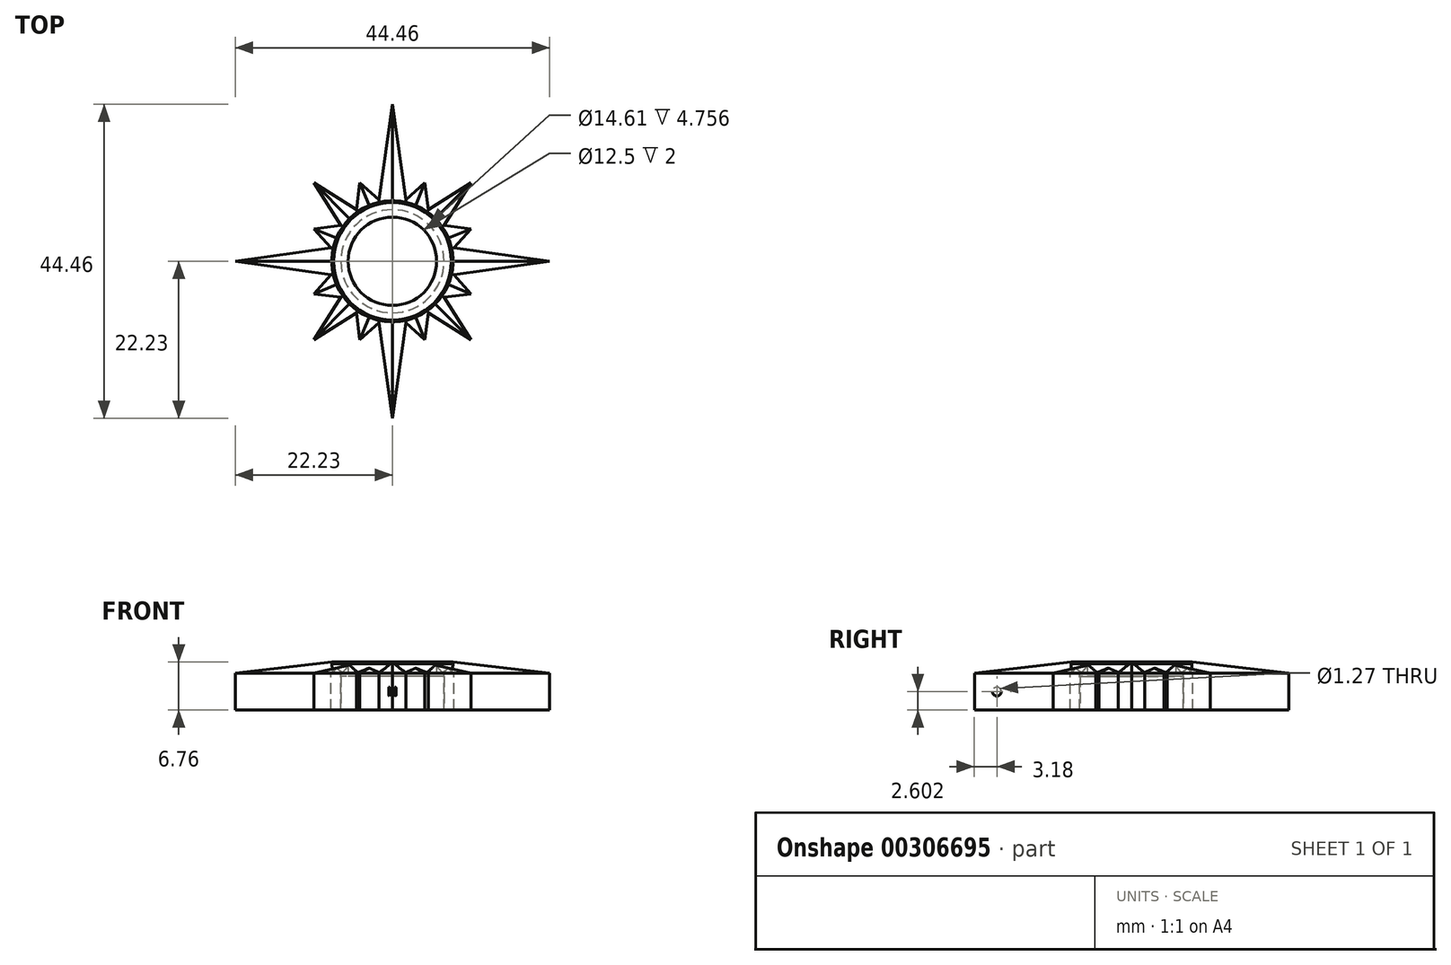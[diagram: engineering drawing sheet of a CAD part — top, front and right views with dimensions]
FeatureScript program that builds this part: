
annotation { "Feature Type Name" : "Feature", "Feature Type Description" : "" }
export const myFeature = defineFeature(function(context is Context, id is Id, definition is map)
    precondition{}
    {
        {
            var Q0;
            Q0=qCreatedBy(makeId("Top.planeOp"),FACE);
            var sketch = newSketch(context, id + "F0", { "sketchPlane" : qUnion([Q0])});
            skCircle(sketch, "E0", {"center": v(0, 0) * mm, "radius": 8.9 * mm, "construction": true});
            skCircle(sketch, "E1", {"center": v(0, 0) * mm, "radius": 12.03 * mm, "construction": true});
            skCircle(sketch, "E2", {"center": v(0, 0) * mm, "radius": 15.72 * mm, "construction": true});
            skCircle(sketch, "E3", {"center": v(0, 0) * mm, "radius": 22.23 * mm, "construction": true});
            skLineSegment(sketch, "E4", {"start": v(8.9, 0) * mm, "end": v(22.23, 0) * mm, "construction": true});
            skLineSegment(sketch, "E5", {"start": v(0, 0) * mm, "end": v(0, 22.23) * mm, "construction": true});
            skLineSegment(sketch, "E6", {"start": v(4.72, 21.72) * mm, "end": v(0, 0) * mm, "construction": true});
            skLineSegment(sketch, "E7", {"start": v(0, 0) * mm, "end": v(8.5, 20.53) * mm, "construction": true});
            skLineSegment(sketch, "E8", {"start": v(12.67, 18.26) * mm, "end": v(0, 0) * mm, "construction": true});
            skLineSegment(sketch, "E9", {"start": v(15.72, 15.72) * mm, "end": v(0, 0) * mm, "construction": true});
            skLineSegment(sketch, "E10", {"start": v(0, 22.23) * mm, "end": v(1.89, 8.69) * mm});
            skLineSegment(sketch, "E11", {"start": v(1.89, 8.69) * mm, "end": v(4.6, 11.11) * mm});
            skLineSegment(sketch, "E12", {"start": v(4.6, 11.11) * mm, "end": v(5.07, 7.3) * mm});
            skLineSegment(sketch, "E13", {"start": v(5.07, 7.3) * mm, "end": v(11.11, 11.11) * mm});
            skLineSegment(sketch, "E14.MirrorCS", {"start": v(7.3, 5.07) * mm, "end": v(11.11, 11.11) * mm});
            skLineSegment(sketch, "E15.MirrorCS", {"start": v(11.11, 4.6) * mm, "end": v(7.3, 5.07) * mm});
            skLineSegment(sketch, "E16.MirrorCS", {"start": v(22.23, 0) * mm, "end": v(8.69, 1.89) * mm});
            skLineSegment(sketch, "E17.MirrorCS", {"start": v(8.69, 1.89) * mm, "end": v(11.11, 4.6) * mm});
            skLineSegment(sketch, "E18.MirrorCS", {"start": v(0, -22.23) * mm, "end": v(1.89, -8.69) * mm});
            skLineSegment(sketch, "E19.MirrorCS", {"start": v(1.89, -8.69) * mm, "end": v(4.6, -11.11) * mm});
            skLineSegment(sketch, "E20.MirrorCS", {"start": v(4.6, -11.11) * mm, "end": v(5.07, -7.3) * mm});
            skLineSegment(sketch, "E21.MirrorCS", {"start": v(5.07, -7.3) * mm, "end": v(11.11, -11.11) * mm});
            skLineSegment(sketch, "E22.MirrorCS", {"start": v(7.3, -5.07) * mm, "end": v(11.11, -11.11) * mm});
            skLineSegment(sketch, "E23.MirrorCS", {"start": v(11.11, -4.6) * mm, "end": v(7.3, -5.07) * mm});
            skLineSegment(sketch, "E24.MirrorCS", {"start": v(22.23, 0) * mm, "end": v(8.69, -1.89) * mm});
            skLineSegment(sketch, "E25.MirrorCS", {"start": v(8.69, -1.89) * mm, "end": v(11.11, -4.6) * mm});
            skLineSegment(sketch, "E26.MirrorCS", {"start": v(0, -22.23) * mm, "end": v(-1.89, -8.69) * mm});
            skLineSegment(sketch, "E27.MirrorCS", {"start": v(-1.89, -8.69) * mm, "end": v(-4.6, -11.11) * mm});
            skLineSegment(sketch, "E28.MirrorCS", {"start": v(-4.6, -11.11) * mm, "end": v(-5.07, -7.3) * mm});
            skLineSegment(sketch, "E29.MirrorCS", {"start": v(-5.07, -7.3) * mm, "end": v(-11.11, -11.11) * mm});
            skLineSegment(sketch, "E30.MirrorCS", {"start": v(-7.3, -5.07) * mm, "end": v(-11.11, -11.11) * mm});
            skLineSegment(sketch, "E31.MirrorCS", {"start": v(-11.11, -4.6) * mm, "end": v(-7.3, -5.07) * mm});
            skLineSegment(sketch, "E32.MirrorCS", {"start": v(-8.69, -1.89) * mm, "end": v(-11.11, -4.6) * mm});
            skLineSegment(sketch, "E33.MirrorCS", {"start": v(-22.23, 0) * mm, "end": v(-8.69, -1.89) * mm});
            skLineSegment(sketch, "E34.MirrorCS", {"start": v(-22.23, 0) * mm, "end": v(-8.69, 1.89) * mm});
            skLineSegment(sketch, "E35.MirrorCS", {"start": v(-8.69, 1.89) * mm, "end": v(-11.11, 4.6) * mm});
            skLineSegment(sketch, "E36.MirrorCS", {"start": v(-11.11, 4.6) * mm, "end": v(-7.3, 5.07) * mm});
            skLineSegment(sketch, "E37.MirrorCS", {"start": v(-7.3, 5.07) * mm, "end": v(-11.11, 11.11) * mm});
            skLineSegment(sketch, "E38.MirrorCS", {"start": v(-5.07, 7.3) * mm, "end": v(-11.11, 11.11) * mm});
            skLineSegment(sketch, "E39.MirrorCS", {"start": v(-4.6, 11.11) * mm, "end": v(-5.07, 7.3) * mm});
            skLineSegment(sketch, "E40.MirrorCS", {"start": v(0, 22.23) * mm, "end": v(-1.89, 8.69) * mm});
            skLineSegment(sketch, "E41.MirrorCS", {"start": v(-1.89, 8.69) * mm, "end": v(-4.6, 11.11) * mm});
            skLineSegment(sketch, "E42", {"start": v(4.6, 11.11) * mm, "end": v(11.11, 11.11) * mm, "construction": true});
            skLineSegment(sketch, "E43", {"start": v(0, 22.23) * mm, "end": v(11.11, 11.11) * mm, "construction": true});
            skSolve(sketch);
        }
        {
            var Q0;
            Q0=qCreatedBy(makeId("Top.planeOp"),FACE);
            cPlane(context, id + "F1", {"entities" : qUnion([Q0]), "cplaneType" : CPlaneType.OFFSET, "offset" : 2.54 * mm, "width" : 152.4 * mm, "height" : 152.4 * mm});
        }
        {
            var Q0;
            Q0=qCreatedBy(id+"F1.planeOp",FACE);
            var sketch = newSketch(context, id + "F2", { "sketchPlane" : qUnion([Q0])});
            skPoint(sketch, "E44", {"position": v(0, 0) * mm});
            skSolve(sketch);
        }
        {
            var Q0;
            Q0=sQuery(id+"F2.wireOp",VERTEX,"E44");
            var Q1;
            Q1=makeQuery(id+"F0.imprint","IMPRINT",FACE,{"disambiguationData":[TD([[makeQuery(id+"F0.imprint","IMPRINT",EDGE,{"derivedFrom":sQuery(id+"F0.wireOp",EDGE,"E10")}),-1.0]])]});
            loft(context, id + "F3", {"sheetProfilesArray" : [{ "sheetProfileEntities" : qUnion([Q0]) }, { "sheetProfileEntities" : qUnion([Q1]) }]});
        }
        {
            var Q0;
            Q0=makeQuery(id+"F3.opLoft","CAP_FACE",FACE,{"disambiguationData":[OSD([makeQuery(id+"F0.imprint","IMPRINT",FACE,{"disambiguationData":[TD([[makeQuery(id+"F0.imprint","IMPRINT",EDGE,{"derivedFrom":sQuery(id+"F0.wireOp",EDGE,"E10")}),-1.0]])]})])],"isStart":true});
            var sketch = newSketch(context, id + "F4", { "sketchPlane" : qUnion([Q0])});
            skCircle(sketch, "E45", {"center": v(0, 0) * mm, "radius": 8.57 * mm});
            skSolve(sketch);
        }
        {
            var Q0;
            Q0 = qSketchRegion(id + "F4", true);
            extrude(context, id + "F5", {"entities" : qUnion([Q0]), "operationType" : NewBodyOperationType.REMOVE, "endBound" : BoundingType.THROUGH_ALL, "oppositeDirection" : true, "depth" : 25.4 * mm});
        }
        {
            var Q0;
            Q0 = qSketchRegion(id + "F0", true);
            extrude(context, id + "F6", {"entities" : qUnion([Q0]), "operationType" : NewBodyOperationType.ADD, "oppositeDirection" : true, "depth" : 5.2 * mm});
        }
        {
            var Q0;
            Q0=makeQuery(id+"F6.opExtrude","CAP_FACE",FACE,{"disambiguationData":[OSD([sQuery(id+"F0.wireOp",EDGE,"E10"),sQuery(id+"F0.wireOp",EDGE,"E11"),sQuery(id+"F0.wireOp",EDGE,"E12"),sQuery(id+"F0.wireOp",EDGE,"E13"),sQuery(id+"F0.wireOp",EDGE,"E14.MirrorCS"),sQuery(id+"F0.wireOp",EDGE,"E15.MirrorCS"),sQuery(id+"F0.wireOp",EDGE,"E16.MirrorCS"),sQuery(id+"F0.wireOp",EDGE,"E17.MirrorCS"),sQuery(id+"F0.wireOp",EDGE,"E18.MirrorCS"),sQuery(id+"F0.wireOp",EDGE,"E19.MirrorCS"),sQuery(id+"F0.wireOp",EDGE,"E20.MirrorCS"),sQuery(id+"F0.wireOp",EDGE,"E21.MirrorCS"),sQuery(id+"F0.wireOp",EDGE,"E22.MirrorCS"),sQuery(id+"F0.wireOp",EDGE,"E23.MirrorCS"),sQuery(id+"F0.wireOp",EDGE,"E24.MirrorCS"),sQuery(id+"F0.wireOp",EDGE,"E25.MirrorCS"),sQuery(id+"F0.wireOp",EDGE,"E26.MirrorCS"),sQuery(id+"F0.wireOp",EDGE,"E27.MirrorCS"),sQuery(id+"F0.wireOp",EDGE,"E28.MirrorCS"),sQuery(id+"F0.wireOp",EDGE,"E29.MirrorCS"),sQuery(id+"F0.wireOp",EDGE,"E30.MirrorCS"),sQuery(id+"F0.wireOp",EDGE,"E31.MirrorCS"),sQuery(id+"F0.wireOp",EDGE,"E32.MirrorCS"),sQuery(id+"F0.wireOp",EDGE,"E33.MirrorCS"),sQuery(id+"F0.wireOp",EDGE,"E34.MirrorCS"),sQuery(id+"F0.wireOp",EDGE,"E35.MirrorCS"),sQuery(id+"F0.wireOp",EDGE,"E36.MirrorCS"),sQuery(id+"F0.wireOp",EDGE,"E37.MirrorCS"),sQuery(id+"F0.wireOp",EDGE,"E38.MirrorCS"),sQuery(id+"F0.wireOp",EDGE,"E39.MirrorCS"),sQuery(id+"F0.wireOp",EDGE,"E40.MirrorCS"),sQuery(id+"F0.wireOp",EDGE,"E41.MirrorCS")])],"isStart":false});
            var sketch = newSketch(context, id + "F7", { "sketchPlane" : qUnion([Q0])});
            skCircle(sketch, "E46", {"center": v(0, 0) * mm, "radius": 7.3 * mm});
            skSolve(sketch);
        }
        {
            var Q0;
            Q0 = qSketchRegion(id + "F7", true);
            extrude(context, id + "F8", {"entities" : qUnion([Q0]), "operationType" : NewBodyOperationType.REMOVE, "endBound" : BoundingType.THROUGH_ALL, "oppositeDirection" : true, "depth" : 25.4 * mm});
        }
        {
            var Q0;
            Q0=makeQuery(id+"F6.opExtrude","CAP_FACE",FACE,{"disambiguationData":[OSD([sQuery(id+"F0.wireOp",EDGE,"E10"),sQuery(id+"F0.wireOp",EDGE,"E11"),sQuery(id+"F0.wireOp",EDGE,"E12"),sQuery(id+"F0.wireOp",EDGE,"E13"),sQuery(id+"F0.wireOp",EDGE,"E14.MirrorCS"),sQuery(id+"F0.wireOp",EDGE,"E15.MirrorCS"),sQuery(id+"F0.wireOp",EDGE,"E16.MirrorCS"),sQuery(id+"F0.wireOp",EDGE,"E17.MirrorCS"),sQuery(id+"F0.wireOp",EDGE,"E18.MirrorCS"),sQuery(id+"F0.wireOp",EDGE,"E19.MirrorCS"),sQuery(id+"F0.wireOp",EDGE,"E20.MirrorCS"),sQuery(id+"F0.wireOp",EDGE,"E21.MirrorCS"),sQuery(id+"F0.wireOp",EDGE,"E22.MirrorCS"),sQuery(id+"F0.wireOp",EDGE,"E23.MirrorCS"),sQuery(id+"F0.wireOp",EDGE,"E24.MirrorCS"),sQuery(id+"F0.wireOp",EDGE,"E25.MirrorCS"),sQuery(id+"F0.wireOp",EDGE,"E26.MirrorCS"),sQuery(id+"F0.wireOp",EDGE,"E27.MirrorCS"),sQuery(id+"F0.wireOp",EDGE,"E28.MirrorCS"),sQuery(id+"F0.wireOp",EDGE,"E29.MirrorCS"),sQuery(id+"F0.wireOp",EDGE,"E30.MirrorCS"),sQuery(id+"F0.wireOp",EDGE,"E31.MirrorCS"),sQuery(id+"F0.wireOp",EDGE,"E32.MirrorCS"),sQuery(id+"F0.wireOp",EDGE,"E33.MirrorCS"),sQuery(id+"F0.wireOp",EDGE,"E34.MirrorCS"),sQuery(id+"F0.wireOp",EDGE,"E35.MirrorCS"),sQuery(id+"F0.wireOp",EDGE,"E36.MirrorCS"),sQuery(id+"F0.wireOp",EDGE,"E37.MirrorCS"),sQuery(id+"F0.wireOp",EDGE,"E38.MirrorCS"),sQuery(id+"F0.wireOp",EDGE,"E39.MirrorCS"),sQuery(id+"F0.wireOp",EDGE,"E40.MirrorCS"),sQuery(id+"F0.wireOp",EDGE,"E41.MirrorCS")])],"isStart":true});
            var sketch = newSketch(context, id + "F9", { "sketchPlane" : qUnion([Q0])});
            skCircle(sketch, "E47", {"center": v(0, 0) * mm, "radius": 6.25 * mm});
            skCircle(sketch, "E48", {"center": v(0, 0) * mm, "radius": 8.57 * mm});
            skSolve(sketch);
        }
        {
            var Q0;
            Q0 = qSketchRegion(id + "F9", true);
            extrude(context, id + "F10", {"entities" : qUnion([Q0]), "operationType" : NewBodyOperationType.ADD, "depth" : 1.56 * mm, "hasSecondDirection" : true, "secondDirectionOppositeDirection" : true, "secondDirectionDepth" : 2 * mm - (1.56 * mm)});
        }
        {
            var Q0;
            Q0=qCreatedBy(makeId("Right.planeOp"),FACE);
            var sketch = newSketch(context, id + "F11", { "sketchPlane" : qUnion([Q0])});
            skCircle(sketch, "E49", {"center": v(-19.05, -2.6) * mm, "radius": 0.64 * mm});
            skSolve(sketch);
        }
        {
            var Q0;
            Q0 = qSketchRegion(id + "F11", true);
            extrude(context, id + "F12", {"entities" : qUnion([Q0]), "operationType" : NewBodyOperationType.REMOVE, "endBound" : BoundingType.THROUGH_ALL, "depth" : 25.4 * mm, "hasSecondDirection" : true, "secondDirectionBound" : SecondDirectionBoundingType.THROUGH_ALL, "secondDirectionOppositeDirection" : true, "secondDirectionDepth" : 25.4 * mm});
        }
        {
            var Q0;
            {var subQ0=sQuery(id+"F9.wireOp",EDGE,"E48");var subQ1=makeQuery(id+"F10.opExtrude","CAP_FACE",FACE,{"disambiguationData":[OSD([sQuery(id+"F9.wireOp",EDGE,"E47"),subQ0])],"isStart":false});var subQ2=makeQuery(id+"F10.opExtrude","SWEPT_FACE",FACE,{"disambiguationData":[OSD([subQ0])]});Q0=makeQuery(id+"F10.boolean.opBoolean","SPLIT",EDGE,{"disambiguationData":[topologyDisambiguationEdgeConnected([subQ1,subQ2]),TD([makeQuery(id+"F3.opLoft","SWEPT_FACE",FACE,{"disambiguationData":[OSD([sQuery(id+"F0.wireOp",EDGE,"E18.MirrorCS"),sQuery(id+"F0.wireOp",EDGE,"E26.MirrorCS"),sQuery(id+"F0.wireOp",EDGE,"E27.MirrorCS")])]})])],"derivedFrom":makeQuery(id+"F10.opExtrude","CAP_EDGE",EDGE,{"disambiguationData":[OSD([subQ0])],"isStart":false})});}
            var Q1;
            {var subQ0=sQuery(id+"F9.wireOp",EDGE,"E48");var subQ1=makeQuery(id+"F10.opExtrude","CAP_FACE",FACE,{"disambiguationData":[OSD([sQuery(id+"F9.wireOp",EDGE,"E47"),subQ0])],"isStart":false});var subQ2=makeQuery(id+"F10.opExtrude","SWEPT_FACE",FACE,{"disambiguationData":[OSD([subQ0])]});Q1=makeQuery(id+"F10.boolean.opBoolean","SPLIT",EDGE,{"disambiguationData":[topologyDisambiguationEdgeConnected([subQ1,subQ2]),TD([makeQuery(id+"F3.opLoft","SWEPT_FACE",FACE,{"disambiguationData":[OSD([sQuery(id+"F0.wireOp",EDGE,"E16.MirrorCS"),sQuery(id+"F0.wireOp",EDGE,"E24.MirrorCS"),sQuery(id+"F0.wireOp",EDGE,"E25.MirrorCS")])]})])],"derivedFrom":makeQuery(id+"F10.opExtrude","CAP_EDGE",EDGE,{"disambiguationData":[OSD([subQ0])],"isStart":false})});}
            var Q2;
            {var subQ0=sQuery(id+"F9.wireOp",EDGE,"E48");var subQ1=makeQuery(id+"F10.opExtrude","CAP_FACE",FACE,{"disambiguationData":[OSD([sQuery(id+"F9.wireOp",EDGE,"E47"),subQ0])],"isStart":false});var subQ2=makeQuery(id+"F10.opExtrude","SWEPT_FACE",FACE,{"disambiguationData":[OSD([subQ0])]});Q2=makeQuery(id+"F10.boolean.opBoolean","SPLIT",EDGE,{"disambiguationData":[topologyDisambiguationEdgeConnected([subQ1,subQ2]),TD([makeQuery(id+"F3.opLoft","SWEPT_FACE",FACE,{"disambiguationData":[OSD([sQuery(id+"F0.wireOp",EDGE,"E10"),sQuery(id+"F0.wireOp",EDGE,"E11"),sQuery(id+"F0.wireOp",EDGE,"E40.MirrorCS")])]})])],"derivedFrom":makeQuery(id+"F10.opExtrude","CAP_EDGE",EDGE,{"disambiguationData":[OSD([subQ0])],"isStart":false})});}
            var Q3;
            {var subQ0=sQuery(id+"F9.wireOp",EDGE,"E48");var subQ1=makeQuery(id+"F10.opExtrude","CAP_FACE",FACE,{"disambiguationData":[OSD([sQuery(id+"F9.wireOp",EDGE,"E47"),subQ0])],"isStart":false});var subQ2=makeQuery(id+"F10.opExtrude","SWEPT_FACE",FACE,{"disambiguationData":[OSD([subQ0])]});Q3=makeQuery(id+"F10.boolean.opBoolean","SPLIT",EDGE,{"disambiguationData":[topologyDisambiguationEdgeConnected([subQ1,subQ2]),TD([makeQuery(id+"F3.opLoft","SWEPT_FACE",FACE,{"disambiguationData":[OSD([sQuery(id+"F0.wireOp",EDGE,"E10"),sQuery(id+"F0.wireOp",EDGE,"E40.MirrorCS"),sQuery(id+"F0.wireOp",EDGE,"E41.MirrorCS")])]})])],"derivedFrom":makeQuery(id+"F10.opExtrude","CAP_EDGE",EDGE,{"disambiguationData":[OSD([subQ0])],"isStart":false})});}
            chamfer(context, id + "F13", {"entities" : qUnion([Q0, Q1, Q2, Q3]), "width" : 0.25 * mm, "tangentPropagation" : true});
        }
    });
